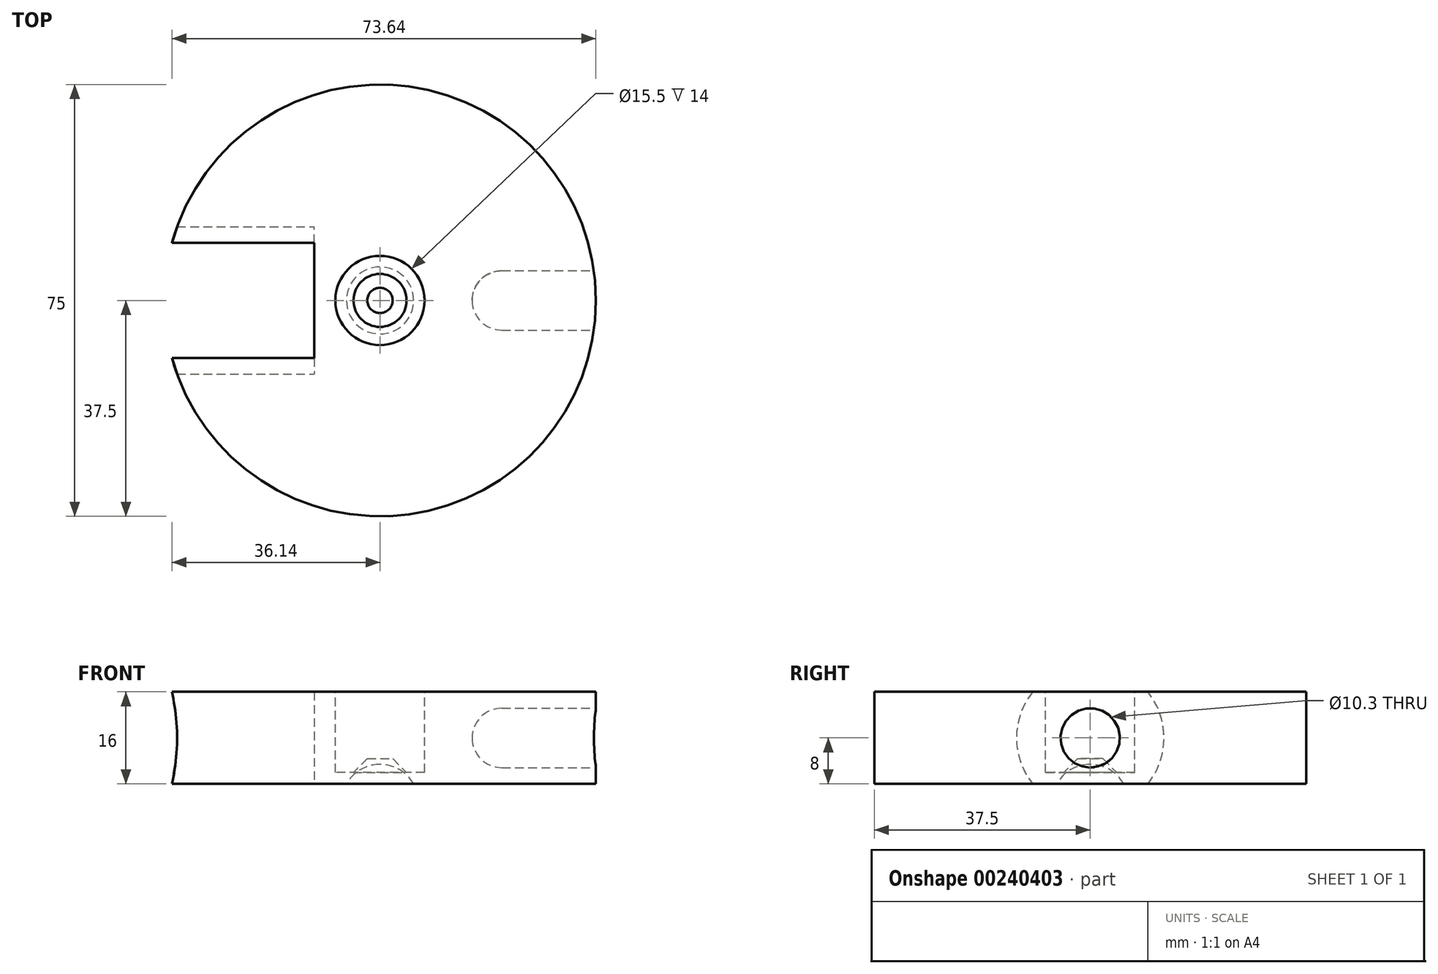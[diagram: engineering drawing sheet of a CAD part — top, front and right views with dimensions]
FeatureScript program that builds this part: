
annotation { "Feature Type Name" : "Feature", "Feature Type Description" : "" }
export const myFeature = defineFeature(function(context is Context, id is Id, definition is map)
    precondition{}
    {
        {
            var Q0;
            Q0=qCreatedBy(makeId("Top.planeOp"),FACE);
            var sketch = newSketch(context, id + "F0", { "sketchPlane" : qUnion([Q0])});
            skCircle(sketch, "E0", {"center": v(0, 0) * mm, "radius": 37.5 * mm});
            skSolve(sketch);
        }
        {
            var Q0;
            Q0 = qSketchRegion(id + "F0", true);
            extrude(context, id + "F1", {"entities" : qUnion([Q0]), "depth" : 16 * mm});
        }
        {
            var Q0;
            Q0=qCreatedBy(makeId("Right.planeOp"),FACE);
            var sketch = newSketch(context, id + "F2", { "sketchPlane" : qUnion([Q0])});
            skCircle(sketch, "E1", {"center": v(0, 8) * mm, "radius": 12.8 * mm});
            skSolve(sketch);
        }
        {
            var Q0;
            Q0 = qSketchRegion(id + "F2", true);
            extrude(context, id + "F3", {"entities" : qUnion([Q0]), "operationType" : NewBodyOperationType.REMOVE, "oppositeDirection" : true, "depth" : 40 * mm, "hasSecondDirection" : true, "secondDirectionOppositeDirection" : true, "secondDirectionDepth" : (36.4 - 25) * mm});
        }
        {
            var Q0;
            Q0=makeQuery(id+"F1.opExtrude","CAP_FACE",FACE,{"disambiguationData":[OSD([sQuery(id+"F0.wireOp",EDGE,"E0")])],"isStart":false});
            var sketch = newSketch(context, id + "F4", { "sketchPlane" : qUnion([Q0])});
            skCircle(sketch, "E2", {"center": v(0, 0) * mm, "radius": 7.75 * mm});
            skSolve(sketch);
        }
        {
            var Q0;
            Q0 = qSketchRegion(id + "F4", true);
            extrude(context, id + "F5", {"entities" : qUnion([Q0]), "operationType" : NewBodyOperationType.REMOVE, "oppositeDirection" : true, "depth" : 14 * mm});
        }
        {
            var Q0;
            Q0=makeQuery(id+"F1.opExtrude","CAP_FACE",FACE,{"disambiguationData":[OSD([sQuery(id+"F0.wireOp",EDGE,"E0")])],"isStart":false});
            cPlane(context, id + "F6", {"entities" : qUnion([Q0]), "cplaneType" : CPlaneType.OFFSET, "offset" : 8 * mm, "oppositeDirection" : true, "width" : 150 * mm, "height" : 150 * mm});
        }
        {
            var Q0;
            Q0=qCreatedBy(makeId("Front.planeOp"),FACE);
            var sketch = newSketch(context, id + "F7", { "sketchPlane" : qUnion([Q0])});
            skLineSegment(sketch, "E3", {"start": v(0, 4.4) * mm, "end": v(-2.2, 4.4) * mm});
            skLineSegment(sketch, "E4", {"start": v(-2.2, 4.4) * mm, "end": v(-4.6, 2) * mm});
            skLineSegment(sketch, "E5", {"start": v(-4.6, 2) * mm, "end": v(0, 2) * mm});
            skLineSegment(sketch, "E6", {"start": v(0, 2) * mm, "end": v(0, 4.4) * mm});
            skSolve(sketch);
        }
        {
            var Q0;
            Q0 = qSketchRegion(id + "F7", true);
            var Q1;
            Q1=sQuery(id+"F7.wireOp",EDGE,"E6");
            revolve(context, id + "F8", {"operationType" : NewBodyOperationType.ADD, "entities" : qUnion([Q0]), "axis" : qUnion([Q1]), "revolveType" : RevolveType.FULL});
        }
        {
            var Q0;
            Q0=qCreatedBy(makeId("Front.planeOp"),FACE);
            var sketch = newSketch(context, id + "F9", { "sketchPlane" : qUnion([Q0])});
            skCircle(sketch, "E7", {"center": v(0, -3.3) * mm, "radius": 6.7 * mm});
            skLineSegment(sketch, "E8", {"start": v(0, 3.4) * mm, "end": v(0, -10) * mm});
            skSolve(sketch);
        }
        {
            var Q0;
            {var subQ0=sQuery(id+"F9.wireOp",EDGE,"E8");Q0=makeQuery(id+"F9.imprint","IMPRINT",FACE,{"disambiguationData":[TD([[makeQuery(id+"F9.imprint","IMPRINT",EDGE,{"derivedFrom":subQ0}),1.0]])]});}
            var Q1;
            Q1=sQuery(id+"F9.wireOp",EDGE,"E8");
            revolve(context, id + "F10", {"operationType" : NewBodyOperationType.REMOVE, "entities" : qUnion([Q0]), "axis" : qUnion([Q1]), "revolveType" : RevolveType.FULL, "oppositeDirection" : true});
        }
        {
            var Q0;
            Q0=qCreatedBy(id+"F6.planeOp",FACE);
            var sketch = newSketch(context, id + "F11", { "sketchPlane" : qUnion([Q0])});
            skLineSegment(sketch, "E9.bottom", {"start": v(52, -5.15) * mm, "end": v(21.15, -5.15) * mm});
            skLineSegment(sketch, "E9.top", {"start": v(52, 5.15) * mm, "end": v(21.15, 5.15) * mm});
            skLineSegment(sketch, "E9.left", {"start": v(52, -5.15) * mm, "end": v(52, 5.15) * mm});
            skLineSegment(sketch, "E9.right", {"start": v(16, 0) * mm, "end": v(16, 0) * mm});
            skPoint(sketch, "E9.middle", {"position": v(34, 0) * mm});
            skPoint(sketch, "E10.visualSharp", {"position": v(16, 5.15) * mm});
            skArc(sketch, "E10.filletArc", {"start": v(21.15, 5.15) * mm, "mid": v(17.5, 3.64) * mm, "end": v(16, 0) * mm});
            skPoint(sketch, "E11.visualSharp", {"position": v(16, -5.15) * mm});
            skArc(sketch, "E11.filletArc", {"start": v(16, 0) * mm, "mid": v(17.5, -3.64) * mm, "end": v(21.15, -5.15) * mm});
            skLineSegment(sketch, "E12", {"start": v(16, 0) * mm, "end": v(52, 0) * mm});
            skSolve(sketch);
        }
        {
            var Q0;
            {var subQ0=sQuery(id+"F11.wireOp",EDGE,"E9.top");Q0=makeQuery(id+"F11.imprint","IMPRINT",FACE,{"disambiguationData":[TD([[makeQuery(id+"F11.imprint","IMPRINT",EDGE,{"derivedFrom":subQ0}),1.0]])]});}
            var Q1;
            Q1=sQuery(id+"F11.wireOp",EDGE,"E12");
            revolve(context, id + "F12", {"operationType" : NewBodyOperationType.REMOVE, "entities" : qUnion([Q0]), "axis" : qUnion([Q1]), "revolveType" : RevolveType.FULL, "oppositeDirection" : true});
        }
    });
